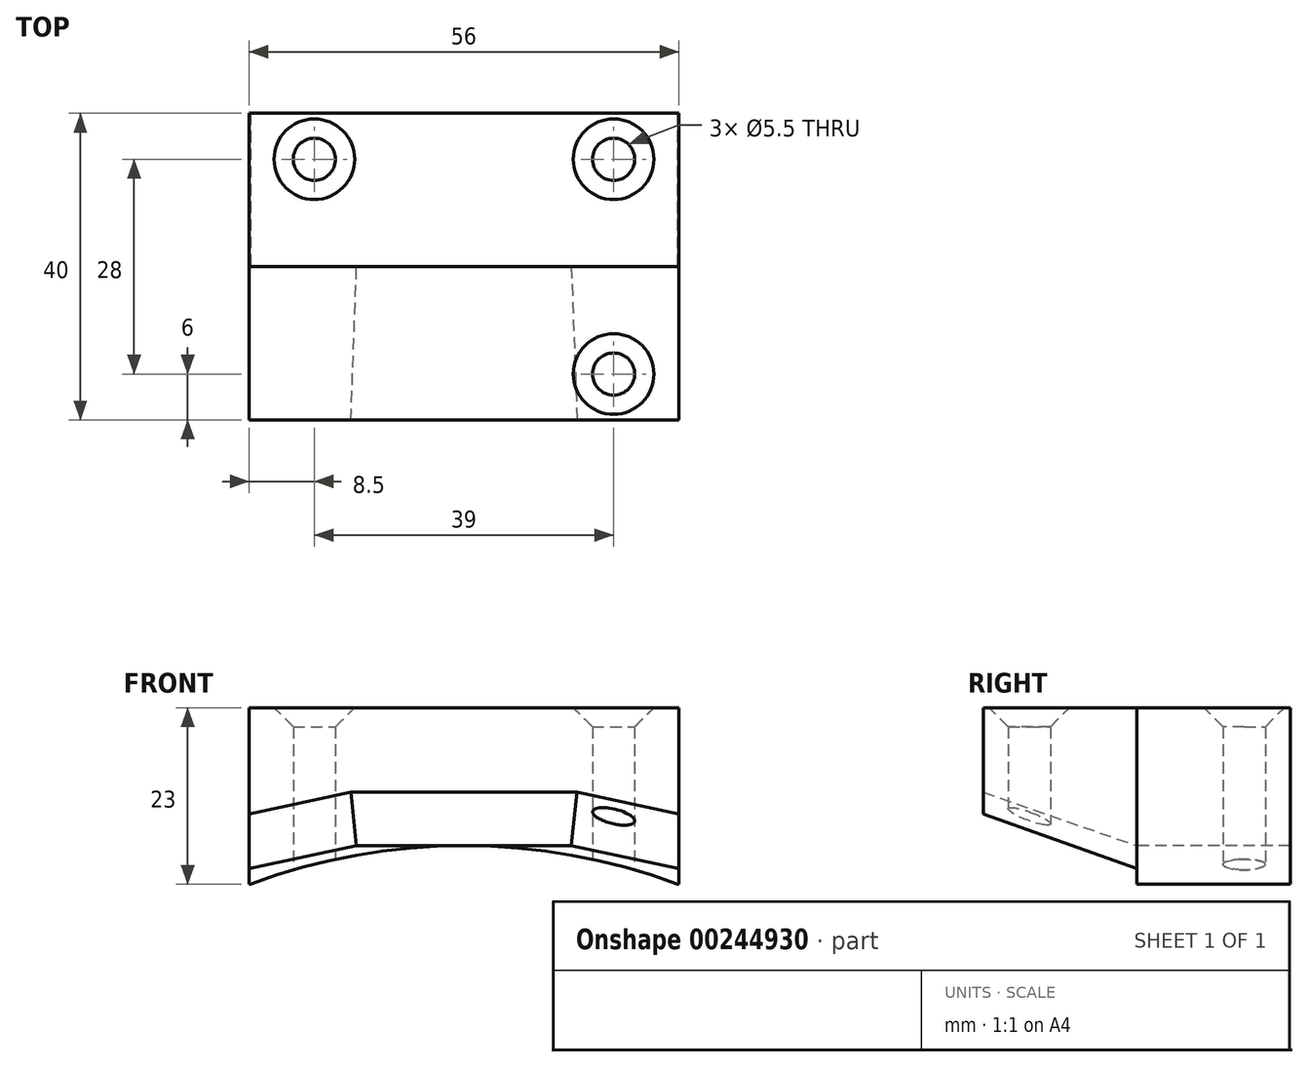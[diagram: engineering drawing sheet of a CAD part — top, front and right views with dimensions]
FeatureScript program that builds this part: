
annotation { "Feature Type Name" : "Feature", "Feature Type Description" : "" }
export const myFeature = defineFeature(function(context is Context, id is Id, definition is map)
    precondition{}
    {
        {
            var Q0;
            Q0=qCreatedBy(makeId("Top.planeOp"),FACE);
            var sketch = newSketch(context, id + "F0", { "sketchPlane" : qUnion([Q0])});
            skPoint(sketch, "E0.middle", {"position": v(0, 0) * mm});
            skLineSegment(sketch, "E1", {"start": v(0, 0) * mm, "end": v(19.5, 0) * mm});
            skLineSegment(sketch, "E2", {"start": v(19.5, 0) * mm, "end": v(19.5, 14) * mm});
            skCircle(sketch, "E3", {"center": v(19.5, 14) * mm, "radius": 2.75 * mm});
            skCircle(sketch, "E4.MirrorC", {"center": v(-19.5, 14) * mm, "radius": 2.75 * mm});
            skLineSegment(sketch, "E5.bottom", {"start": v(28, 0) * mm, "end": v(-28, 0) * mm});
            skLineSegment(sketch, "E5.top", {"start": v(28, 20) * mm, "end": v(-28, 20) * mm});
            skLineSegment(sketch, "E5.left", {"start": v(28, 0) * mm, "end": v(28, 20) * mm});
            skLineSegment(sketch, "E5.right", {"start": v(-28, 0) * mm, "end": v(-28, 20) * mm});
            skPoint(sketch, "E5.middle", {"position": v(0, 10) * mm});
            skLineSegment(sketch, "E6", {"start": v(0, 10) * mm, "end": v(0, 0) * mm});
            skSolve(sketch);
        }
        {
            var Q0;
            Q0 = qSketchRegion(id + "F0", true);
            extrude(context, id + "F1", {"entities" : qUnion([Q0]), "depth" : 23 * mm});
        }
        {
            var Q0;
            Q0=qCreatedBy(makeId("Front.planeOp"),FACE);
            var sketch = newSketch(context, id + "F2", { "sketchPlane" : qUnion([Q0])});
            skLineSegment(sketch, "E7", {"start": v(0, 0) * mm, "end": v(0, -75) * mm});
            skCircle(sketch, "E8", {"center": v(0, -75) * mm, "radius": 80 * mm});
            skSolve(sketch);
        }
        {
            var Q0;
            Q0 = qSketchRegion(id + "F2", true);
            extrude(context, id + "F3", {"entities" : qUnion([Q0]), "oppositeDirection" : true, "depth" : 25 * mm});
        }
        {
            var Q0;
            Q0=qCreatedBy(makeId("Front.planeOp"),FACE);
            var sketch = newSketch(context, id + "F4", { "sketchPlane" : qUnion([Q0])});
            skLineSegment(sketch, "E9", {"start": v(0, 0) * mm, "end": v(0, 5) * mm});
            skLineSegment(sketch, "E10", {"start": v(0, 5) * mm, "end": v(14, 5) * mm});
            skLineSegment(sketch, "E11", {"start": v(14, 5) * mm, "end": v(28, 2) * mm});
            skLineSegment(sketch, "E12", {"start": v(28, 2) * mm, "end": v(28, 23) * mm});
            skLineSegment(sketch, "E13", {"start": v(28, 23) * mm, "end": v(0, 23) * mm});
            skLineSegment(sketch, "E14", {"start": v(0, 23) * mm, "end": v(0, 5) * mm});
            skLineSegment(sketch, "E15.MirrorCS", {"start": v(-28, 23) * mm, "end": v(0, 23) * mm});
            skLineSegment(sketch, "E16.MirrorCS", {"start": v(-28, 2) * mm, "end": v(-28, 23) * mm});
            skLineSegment(sketch, "E17.MirrorCS", {"start": v(-14, 5) * mm, "end": v(-28, 2) * mm});
            skLineSegment(sketch, "E18.MirrorCS", {"start": v(0, 5) * mm, "end": v(-14, 5) * mm});
            skSolve(sketch);
        }
        {
            var Q0;
            Q0 = qSketchRegion(id + "F4", true);
            extrude(context, id + "F5", {"entities" : qUnion([Q0]), "depth" : 20 * mm});
        }
        {
            var Q0;
            Q0=qCreatedBy(makeId("Top.planeOp"),FACE);
            var sketch = newSketch(context, id + "F6", { "sketchPlane" : qUnion([Q0])});
            skLineSegment(sketch, "E19", {"start": v(0, 0) * mm, "end": v(0, -14) * mm});
            skLineSegment(sketch, "E20", {"start": v(0, -14) * mm, "end": v(19.5, -14) * mm});
            skCircle(sketch, "E21", {"center": v(19.5, -14) * mm, "radius": 2.75 * mm});
            skCircle(sketch, "E22.MirrorC", {"center": v(-19.5, -14) * mm, "radius": 2.75 * mm});
            skSolve(sketch);
        }
        {
            var Q0;
            {Q0=qUnion([makeQuery(id+"F6.imprint","IMPRINT",FACE,{"disambiguationData":[TD([[makeQuery(id+"F6.imprint","IMPRINT",EDGE,{"derivedFrom":sQuery(id+"F6.wireOp",EDGE,"E21")}),1.0]])]}),makeQuery(id+"F6.imprint","IMPRINT",FACE,{"disambiguationData":[TD([[makeQuery(id+"F6.imprint","IMPRINT",EDGE,{"derivedFrom":sQuery(id+"F6.wireOp",EDGE,"E22.MirrorC")}),-1.0]])]})]);}
            extrude(context, id + "F7", {"entities" : qUnion([Q0]), "operationType" : NewBodyOperationType.REMOVE, "depth" : 30 * mm});
        }
        {
            var Q0;
            Q0=makeQuery(id+"F5.opExtrude","CAP_EDGE",EDGE,{"disambiguationData":[OSD([sQuery(id+"F4.wireOp",EDGE,"E17.MirrorCS")])],"isStart":false});
            var Q1;
            Q1=makeQuery(id+"F5.opExtrude","CAP_EDGE",EDGE,{"disambiguationData":[OSD([sQuery(id+"F4.wireOp",EDGE,"E10"),sQuery(id+"F4.wireOp",EDGE,"E18.MirrorCS")])],"isStart":false});
            var Q2;
            Q2=makeQuery(id+"F5.opExtrude","CAP_EDGE",EDGE,{"disambiguationData":[OSD([sQuery(id+"F4.wireOp",EDGE,"E11")])],"isStart":false});
            chamfer(context, id + "F8", {"entities" : qUnion([Q0, Q1, Q2]), "chamferType" : ChamferType.TWO_OFFSETS, "width1" : 20 * mm, "oppositeDirection" : false, "width2" : 7 * mm, "tangentPropagation" : true});
        }
        {
            var Q0;
            Q0=makeQuery(id+"F3.opExtrude","SWEPT_BODY",BODY,{"disambiguationData":[OSD([sQuery(id+"F2.wireOp",EDGE,"E8")])]});
            var Q1;
            Q1=makeQuery(id+"F1.opExtrude","SWEPT_BODY",BODY,{"disambiguationData":[OSD([sQuery(id+"F0.wireOp",EDGE,"E3"),sQuery(id+"F0.wireOp",EDGE,"E4.MirrorC"),sQuery(id+"F0.wireOp",EDGE,"E5.bottom"),sQuery(id+"F0.wireOp",EDGE,"E5.top"),sQuery(id+"F0.wireOp",EDGE,"E5.left"),sQuery(id+"F0.wireOp",EDGE,"E5.right")])]});
            booleanBodies(context, id + "F9", {"operationType" : BooleanOperationType.SUBTRACTION, "tools" : qUnion([Q0]), "targets" : qUnion([Q1])});
        }
        {
            var Q0;
            Q0=makeQuery(id+"F7.boolean.opBoolean","INTERSECT",EDGE,{"derivedFrom":[makeQuery(id+"F5.opExtrude","SWEPT_FACE",FACE,{"disambiguationData":[OSD([sQuery(id+"F4.wireOp",EDGE,"E13"),sQuery(id+"F4.wireOp",EDGE,"E15.MirrorCS")])]}),makeQuery(id+"F7.opExtrude","SWEPT_FACE",FACE,{"disambiguationData":[OSD([sQuery(id+"F6.wireOp",EDGE,"E22.MirrorC")])]})]});
            var Q1;
            Q1=makeQuery(id+"F1.opExtrude","CAP_EDGE",EDGE,{"disambiguationData":[OSD([sQuery(id+"F0.wireOp",EDGE,"E4.MirrorC")])],"isStart":false});
            var Q2;
            Q2=makeQuery(id+"F1.opExtrude","CAP_EDGE",EDGE,{"disambiguationData":[OSD([sQuery(id+"F0.wireOp",EDGE,"E3")])],"isStart":false});
            var Q3;
            Q3=makeQuery(id+"F7.boolean.opBoolean","INTERSECT",EDGE,{"derivedFrom":[makeQuery(id+"F5.opExtrude","SWEPT_FACE",FACE,{"disambiguationData":[OSD([sQuery(id+"F4.wireOp",EDGE,"E13"),sQuery(id+"F4.wireOp",EDGE,"E15.MirrorCS")])]}),makeQuery(id+"F7.opExtrude","SWEPT_FACE",FACE,{"disambiguationData":[OSD([sQuery(id+"F6.wireOp",EDGE,"E21")])]})]});
            chamfer(context, id + "F10", {"entities" : qUnion([Q0, Q1, Q2, Q3]), "width" : 2.5 * mm, "tangentPropagation" : true});
        }
    });
